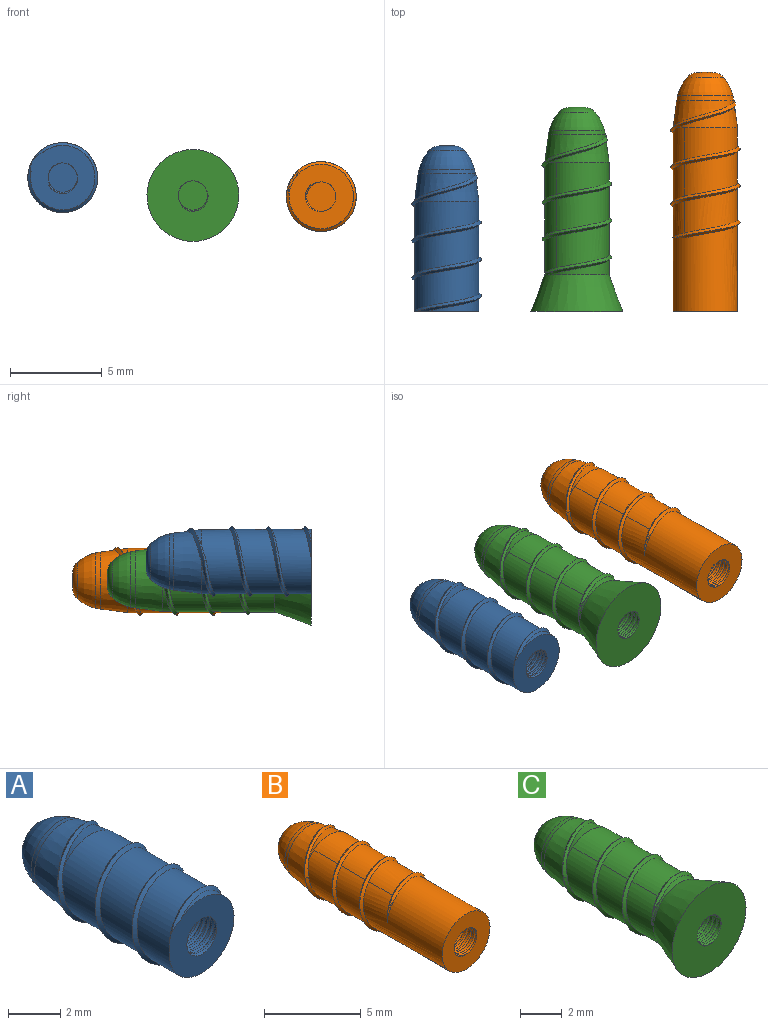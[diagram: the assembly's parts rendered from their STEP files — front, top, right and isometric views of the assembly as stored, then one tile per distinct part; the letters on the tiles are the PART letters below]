
ASSEMBLY  parts=3 mates=2
PART A: 21 faces, bbox 4.1x9.3x4.1 mm
  f0: cylinder r=0.8mm len=6mm, axis (0,-1,0), area 12.4mm2, adj f1,f5,f16,f17,f18,f19
  f1: plane 1.61x1.61mm, normal (0,-1,0), area 2mm2, adj f0,f16,f17,f20
  f2: bspline ~6.18x4.09mm, area 7.3mm2, adj f3,f4,f5,f14
  f3: bspline ~6.15x4.09mm, area 6.4mm2, adj f2,f4,f5,f12
  f4: cylinder r=1.75mm len=6mm, axis (0,1,0), area 57.2mm2, adj f2,f3,f5,f6,f7,f12,f14
  f5: plane 3.56x3.54mm, normal (0,-1,0), area 7.6mm2, adj f0,f2,f3,f4,f17,f18,f19
  f6: cone r=1.75mm half-angle=7.6deg, axis (0,-1,0), area 11.7mm2, adj f4,f7,f8,f13,f14
  f7: cone r=1.75mm half-angle=7.6deg, axis (0,-1,0), area 2.8mm2, adj f4,f6,f12,f15
  f8: cone r=1.35mm half-angle=11.3deg, axis (0,-1,0), area 2.2mm2, adj f6,f10
  f9: plane 0.8x0.8mm, normal (0,1,0), area 0.5mm2, adj f11
  f10: revolved ~3.01x3.01mm, area 9.4mm2, adj f8,f11
  f11: torus R=0.4mm, axis (0,1,0), area 2.9mm2, adj f9,f10
  f12: bspline ~3.57x1.77mm, area 0.8mm2, adj f3,f4,f7,f14,f15
  f13: plane 0.06x0.04mm, normal (-0.04,0.29,-0.95), area 0mm2, adj f6,f14,f15
  f14: bspline ~3.62x2mm, area 1.2mm2, adj f2,f4,f6,f12,f13,f15
  f15: bspline ~0.5x0.35mm, area 0mm2, adj f7,f12,f13,f14
  f16: plane 0.15x0.08mm, normal (0,-0.05,1), area 0mm2, adj f0,f1,f17,f19,f20
  f17: bspline ~6.08x2.02mm, area 13.3mm2, adj f0,f1,f5,f16,f18,f19,f20
  f18: plane 0.02x0.02mm, normal (0,0.05,-1), area 0mm2, adj f0,f5,f17
  f19: bspline ~6.04x2.02mm, area 13.2mm2, adj f0,f5,f16,f17
  f20: bspline ~0.69x0.4mm, area 0mm2, adj f1,f16,f17
PART B: 57 faces, bbox 4.1x13.2x4.1 mm
  f0: bspline ~6.18x4.09mm, area 7.2mm2, adj f1,f2,f3,f4,f5,f6,f15
  f1: bspline ~6.15x4.09mm, area 6.4mm2, adj f0,f2,f3,f4,f6,f13
  f2: cylinder r=1.75mm len=3.73mm, axis (0,1,0), area 19.2mm2, adj f0,f1,f3,f5,f8,f13
  f3: cylinder r=1.75mm len=3.74mm, axis (0,1,0), area 19.1mm2, adj f0,f1,f2,f4
  f4: cylinder r=1.75mm len=6mm, axis (0,1,0), area 54.8mm2, adj f0,f1,f3,f6,f17
  f5: cylinder r=1.75mm len=3.5mm, axis (0,1,0), area 8.3mm2, adj f0,f2,f7,f8,f15
  f6: plane 1.3x0.67mm, normal (0,-1,0), area 0.1mm2, adj f0,f1,f4
  f7: cone r=1.75mm half-angle=7.6deg, axis (0,-1,0), area 11.7mm2, adj f5,f8,f9,f14,f15
  f8: cone r=1.75mm half-angle=7.6deg, axis (0,-1,0), area 2.8mm2, adj f2,f5,f7,f13,f16
  f9: cone r=1.35mm half-angle=11.3deg, axis (0,-1,0), area 2.2mm2, adj f7,f11
  f10: plane 0.8x0.8mm, normal (0,1,0), area 0.5mm2, adj f12
  f11: revolved ~3.01x3.01mm, area 9.4mm2, adj f9,f12
  f12: torus R=0.4mm, axis (0,1,0), area 2.9mm2, adj f10,f11
  f13: bspline ~3.57x1.77mm, area 0.8mm2, adj f1,f2,f8,f15,f16
  f14: plane 0.06x0.04mm, normal (-0.04,0.29,-0.95), area 0mm2, adj f7,f15,f16
  f15: bspline ~3.62x2mm, area 1.2mm2, adj f0,f5,f7,f13,f14,f16
  f16: bspline ~0.5x0.35mm, area 0mm2, adj f8,f13,f14,f15
  f17: plane 3.54x3.54mm, normal (0,-1,0), area 7.5mm2, adj f4,f20,f55,f56
  f18: plane 1.6x1.6mm, normal (0,-1,0), area 2mm2, adj f19
  f19: cylinder r=0.8mm len=1.6mm, axis (0,-1,0), area 1.6mm2, adj f18,f53,f54,f55,f56
  f20: cylinder r=0.8mm len=1.6mm, axis (0,-1,0), area 0.2mm2, adj f17,f21,f55,f56
  f21: cylinder r=0.8mm len=1.6mm, axis (0,-1,0), area 0.7mm2, adj f20,f22,f55,f56
  f22: cylinder r=0.8mm len=1.6mm, axis (0,-1,0), area 0.7mm2, adj f21,f23,f55,f56
  f23: cylinder r=0.8mm len=1.6mm, axis (0,-1,0), area 0.7mm2, adj f22,f24,f55,f56
  f24: cylinder r=0.8mm len=1.6mm, axis (0,-1,0), area 0.7mm2, adj f23,f25,f55,f56
  f25: cylinder r=0.8mm len=1.6mm, axis (0,-1,0), area 0.7mm2, adj f24,f26,f55,f56
  f26: cylinder r=0.8mm len=1.6mm, axis (0,-1,0), area 0.7mm2, adj f25,f27,f55,f56
  f27: cylinder r=0.8mm len=1.6mm, axis (0,-1,0), area 0.7mm2, adj f26,f28,f55,f56
  f28: cylinder r=0.8mm len=1.6mm, axis (0,-1,0), area 0.7mm2, adj f27,f29,f55,f56
  f29: cylinder r=0.8mm len=1.6mm, axis (0,-1,0), area 0.7mm2, adj f28,f30,f55,f56
  f30: cylinder r=0.8mm len=1.6mm, axis (0,-1,0), area 0.7mm2, adj f29,f31,f55,f56
  f31: cylinder r=0.8mm len=1.6mm, axis (0,-1,0), area 0.7mm2, adj f30,f32,f55,f56
  f32: cylinder r=0.8mm len=1.6mm, axis (0,-1,0), area 0.7mm2, adj f31,f33,f55,f56
  f33: cylinder r=0.8mm len=1.6mm, axis (0,-1,0), area 0.7mm2, adj f32,f34,f55,f56
  f34: cylinder r=0.8mm len=1.6mm, axis (0,-1,0), area 0.7mm2, adj f33,f35,f55,f56
  f35: cylinder r=0.8mm len=1.6mm, axis (0,-1,0), area 0.7mm2, adj f34,f36,f55,f56
  f36: cylinder r=0.8mm len=1.6mm, axis (0,-1,0), area 0.7mm2, adj f35,f37,f55,f56
  f37: cylinder r=0.8mm len=1.6mm, axis (0,-1,0), area 0.7mm2, adj f36,f38,f55,f56
  f38: cylinder r=0.8mm len=1.6mm, axis (0,-1,0), area 0.7mm2, adj f37,f39,f55,f56
  f39: cylinder r=0.8mm len=1.6mm, axis (0,-1,0), area 0.7mm2, adj f38,f40,f55,f56
  f40: cylinder r=0.8mm len=1.6mm, axis (0,-1,0), area 0.7mm2, adj f39,f41,f55,f56
  f41: cylinder r=0.8mm len=1.6mm, axis (0,-1,0), area 0.7mm2, adj f40,f42,f55,f56
  f42: cylinder r=0.8mm len=1.6mm, axis (0,-1,0), area 0.7mm2, adj f41,f43,f55,f56
  f43: cylinder r=0.8mm len=1.6mm, axis (0,-1,0), area 0.7mm2, adj f42,f44,f55,f56
  f44: cylinder r=0.8mm len=1.6mm, axis (0,-1,0), area 0.7mm2, adj f43,f45,f55,f56
  f45: cylinder r=0.8mm len=1.6mm, axis (0,-1,0), area 0.7mm2, adj f44,f46,f55,f56
  f46: cylinder r=0.8mm len=1.6mm, axis (0,-1,0), area 0.7mm2, adj f45,f47,f55,f56
  f47: cylinder r=0.8mm len=1.6mm, axis (0,-1,0), area 0.7mm2, adj f46,f48,f55,f56
  f48: cylinder r=0.8mm len=1.6mm, axis (0,-1,0), area 0.7mm2, adj f47,f49,f55,f56
  f49: cylinder r=0.8mm len=1.6mm, axis (0,-1,0), area 0.7mm2, adj f48,f50,f55,f56
  f50: cylinder r=0.8mm len=1.6mm, axis (0,-1,0), area 0.7mm2, adj f49,f51,f55,f56
  f51: cylinder r=0.8mm len=1.6mm, axis (0,-1,0), area 0.7mm2, adj f50,f52,f55,f56
  f52: cylinder r=0.8mm len=1.6mm, axis (0,-1,0), area 0.7mm2, adj f51,f53,f55,f56
  f53: cylinder r=0.8mm len=1.6mm, axis (0,-1,0), area 0.7mm2, adj f19,f52,f55,f56
  f54: plane 0.14x0.07mm, normal (0,-0.06,1), area 0mm2, adj f19,f55,f56
  f55: bspline ~9.98x2.02mm, area 18.6mm2, adj f17,f19,f20,f21,f22,f23,f24,f25
  f56: bspline ~10.03x2.02mm, area 18.7mm2, adj f17,f19,f20,f21,f22,f23,f24,f25
PART C: 26 faces, bbox 5x11.2x5 mm
  f0: cylinder r=0.8mm len=10mm, axis (0,-1,0), area 23.5mm2, adj f1,f19,f21,f22,f23,f25
  f1: plane 1.61x1.61mm, normal (0,-1,0), area 2mm2, adj f0,f21,f24,f25
  f2: bspline ~6.18x4.09mm, area 7.2mm2, adj f3,f4,f5,f6,f7,f8,f17
  f3: bspline ~6.15x4.09mm, area 6.4mm2, adj f2,f4,f5,f6,f8,f15
  f4: cylinder r=1.75mm len=3.73mm, axis (0,1,0), area 19.2mm2, adj f2,f3,f5,f7,f10,f15
  f5: cylinder r=1.75mm len=3.74mm, axis (0,1,0), area 19.1mm2, adj f2,f3,f4,f6
  f6: cylinder r=1.75mm len=3.5mm, axis (0,1,0), area 11.9mm2, adj f2,f3,f5,f8,f20
  f7: cylinder r=1.75mm len=3.5mm, axis (0,1,0), area 8.3mm2, adj f2,f4,f9,f10,f17
  f8: plane 1.3x0.67mm, normal (0,-1,0), area 0.1mm2, adj f2,f3,f6
  f9: cone r=1.75mm half-angle=7.6deg, axis (0,-1,0), area 11.7mm2, adj f7,f10,f11,f16,f17
  f10: cone r=1.75mm half-angle=7.6deg, axis (0,-1,0), area 2.8mm2, adj f4,f7,f9,f15,f18
  f11: cone r=1.35mm half-angle=11.3deg, axis (0,-1,0), area 2.2mm2, adj f9,f13
  f12: plane 0.8x0.8mm, normal (0,1,0), area 0.5mm2, adj f14
  f13: revolved ~3.01x3.01mm, area 9.4mm2, adj f11,f14
  f14: torus R=0.4mm, axis (0,1,0), area 2.9mm2, adj f12,f13
  f15: bspline ~3.57x1.77mm, area 0.8mm2, adj f3,f4,f10,f17,f18
  f16: plane 0.06x0.04mm, normal (-0.04,0.29,-0.95), area 0mm2, adj f9,f17,f18
  f17: bspline ~3.62x2mm, area 1.2mm2, adj f2,f7,f9,f15,f16,f18
  f18: bspline ~0.5x0.35mm, area 0mm2, adj f10,f15,f16,f17
  f19: plane 5.04x5.04mm, normal (0,-1,0), area 17.5mm2, adj f0,f20,f22,f23,f25
  f20: cone r=1.75mm half-angle=20.6deg, axis (0,-1,0), area 28.5mm2, adj f6,f19
  f21: plane 0.15x0.08mm, normal (0,-0.06,1), area 0mm2, adj f0,f1,f23,f24,f25
  f22: plane 0.02x0.02mm, normal (0,0.06,-1), area 0mm2, adj f0,f19,f25
  f23: bspline ~10.03x2.01mm, area 18mm2, adj f0,f19,f21,f25
  f24: bspline ~0.69x0.4mm, area 0mm2, adj f1,f21,f25
  f25: bspline ~10.08x2.01mm, area 18.1mm2, adj f0,f1,f19,f21,f22,f23,f24
PLACE A t=(1.03,-9.29,-0.67)mm
PLACE B t=(15.09,-5.29,-1.7)mm
PLACE C t=(8.11,-7.19,-1.64)mm
MATE planar B.f17 <-> C.f4  axis (0,-1,0) through (14.23,-15.29,-1.86)mm
MATE planar A.f5 <-> B.f17  axis (0,-1,0) through (1,-15.29,-0.65)mm
